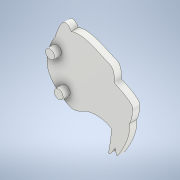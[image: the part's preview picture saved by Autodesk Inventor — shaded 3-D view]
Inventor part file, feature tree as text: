
AUTODESK INVENTOR PART (.ipt)
format: ipt  version: 2022 (Build 260153000, 153)  size: 145,408 bytes
history: native  units: in
note: dims shown in document units (in); Inventor stores cm internally (conversion verified against a paired STEP export)
features: extrude x2, sketch x1
ambient origin geometry x8: Origin, YZ Plane, XZ Plane, XY Plane, X Axis, Y Axis, Z Axis, Center Point
bodies: Solid1 (feature_tree)
feature tree (3):
  sketch  "Sketch2"  dims[d0=0.1969in d1=0.0in d2=0.1969in d3=0.0in]
  extrude  "Extrusion1"  Depth=0.1969in TaperAngle=0.0deg
  extrude  "Extrusion2"  [1 undecoded]
note: 1 required parameter value undecoded (feature->parameter linkage not recoverable at this tier; creation-order binding heuristic only, values carry confidence <= 0.55)
